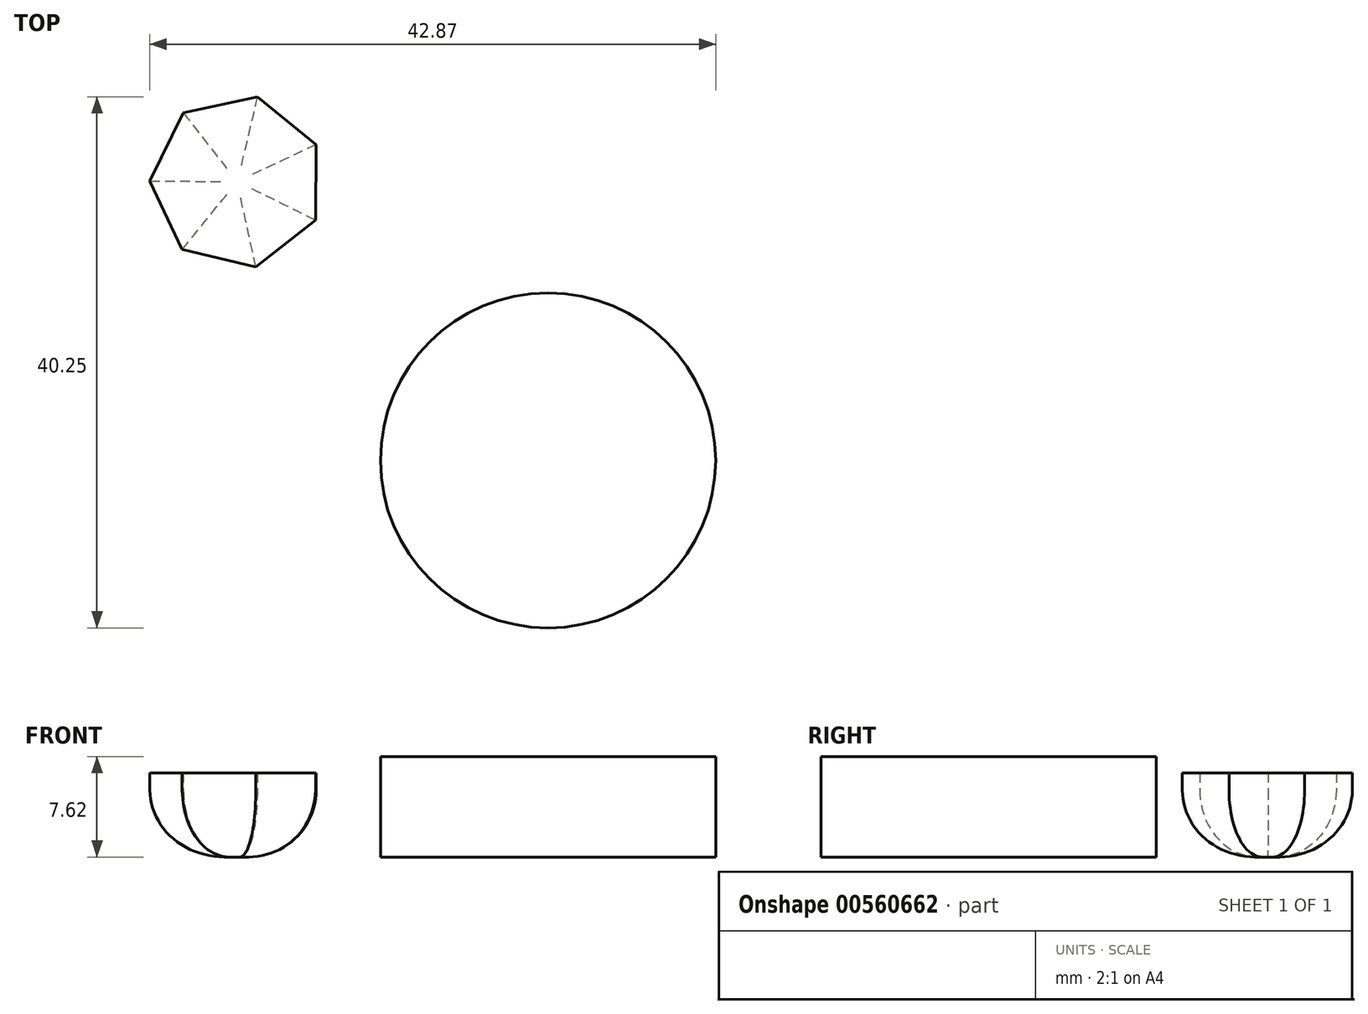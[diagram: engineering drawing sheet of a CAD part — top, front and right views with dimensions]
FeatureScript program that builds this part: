
annotation { "Feature Type Name" : "Feature", "Feature Type Description" : "" }
export const myFeature = defineFeature(function(context is Context, id is Id, definition is map)
    precondition{}
    {
        {
            var Q0;
            Q0=qCreatedBy(makeId("Top.planeOp"),FACE);
            var sketch = newSketch(context, id + "F0", { "sketchPlane" : qUnion([Q0])});
            skCircle(sketch, "E0", {"center": v(-86.15, 13.87) * mm, "radius": 12.7 * mm});
            skSolve(sketch);
        }
        {
            var Q0;
            Q0=makeQuery(id+"F0.imprint","IMPRINT",FACE,{"disambiguationData":[TD([[makeQuery(id+"F0.imprint","IMPRINT",EDGE,{"derivedFrom":sQuery(id+"F0.wireOp",EDGE,"E0")}),1.0]])]});
            extrude(context, id + "F1", {"entities" : qUnion([Q0]), "depth" : 7.62 * mm, "offsetDistance" : 25.4 * mm});
        }
        {
            var Q0;
            Q0=qCreatedBy(makeId("Top.planeOp"),FACE);
            var sketch = newSketch(context, id + "F2", { "sketchPlane" : qUnion([Q0])});
            skCircle(sketch, "E1.cCircle", {"center": v(-109.7, 34.99) * mm, "radius": 5.96 * mm, "construction": true});
            skLineSegment(sketch, "E1.0", {"start": v(-113.78, 40.2) * mm, "end": v(-108.17, 41.42) * mm});
            skLineSegment(sketch, "E1.1", {"start": v(-108.17, 41.42) * mm, "end": v(-103.72, 37.8) * mm});
            skLineSegment(sketch, "E1.2", {"start": v(-103.72, 37.8) * mm, "end": v(-103.77, 32.06) * mm});
            skLineSegment(sketch, "E1.3", {"start": v(-103.77, 32.06) * mm, "end": v(-108.29, 28.52) * mm});
            skLineSegment(sketch, "E1.4", {"start": v(-108.29, 28.52) * mm, "end": v(-113.87, 29.85) * mm});
            skLineSegment(sketch, "E1.5", {"start": v(-113.87, 29.85) * mm, "end": v(-116.32, 35.04) * mm});
            skLineSegment(sketch, "E1.6", {"start": v(-116.32, 35.04) * mm, "end": v(-113.78, 40.2) * mm});
            skPoint(sketch, "E1.0.midPoint", {"position": v(-110.98, 40.8) * mm});
            skSolve(sketch);
        }
        {
            var Q0;
            Q0 = qSketchRegion(id + "F2", true);
            extrude(context, id + "F3", {"entities" : qUnion([Q0]), "depth" : 6.38 * mm, "offsetDistance" : 25.4 * mm});
        }
        {
            var Q0;
            Q0=makeQuery(id+"F3.opExtrude","CAP_FACE",FACE,{"disambiguationData":[OSD([sQuery(id+"F2.wireOp",EDGE,"E1.0"),sQuery(id+"F2.wireOp",EDGE,"E1.1"),sQuery(id+"F2.wireOp",EDGE,"E1.2"),sQuery(id+"F2.wireOp",EDGE,"E1.3"),sQuery(id+"F2.wireOp",EDGE,"E1.4"),sQuery(id+"F2.wireOp",EDGE,"E1.5"),sQuery(id+"F2.wireOp",EDGE,"E1.6")])],"isStart":true});
            fillet(context, id + "F4", {"entities" : qUnion([Q0]), "radius" : 5.08 * mm, "tangentPropagation" : true, "allowEdgeOverflow" : false});
        }
    });
